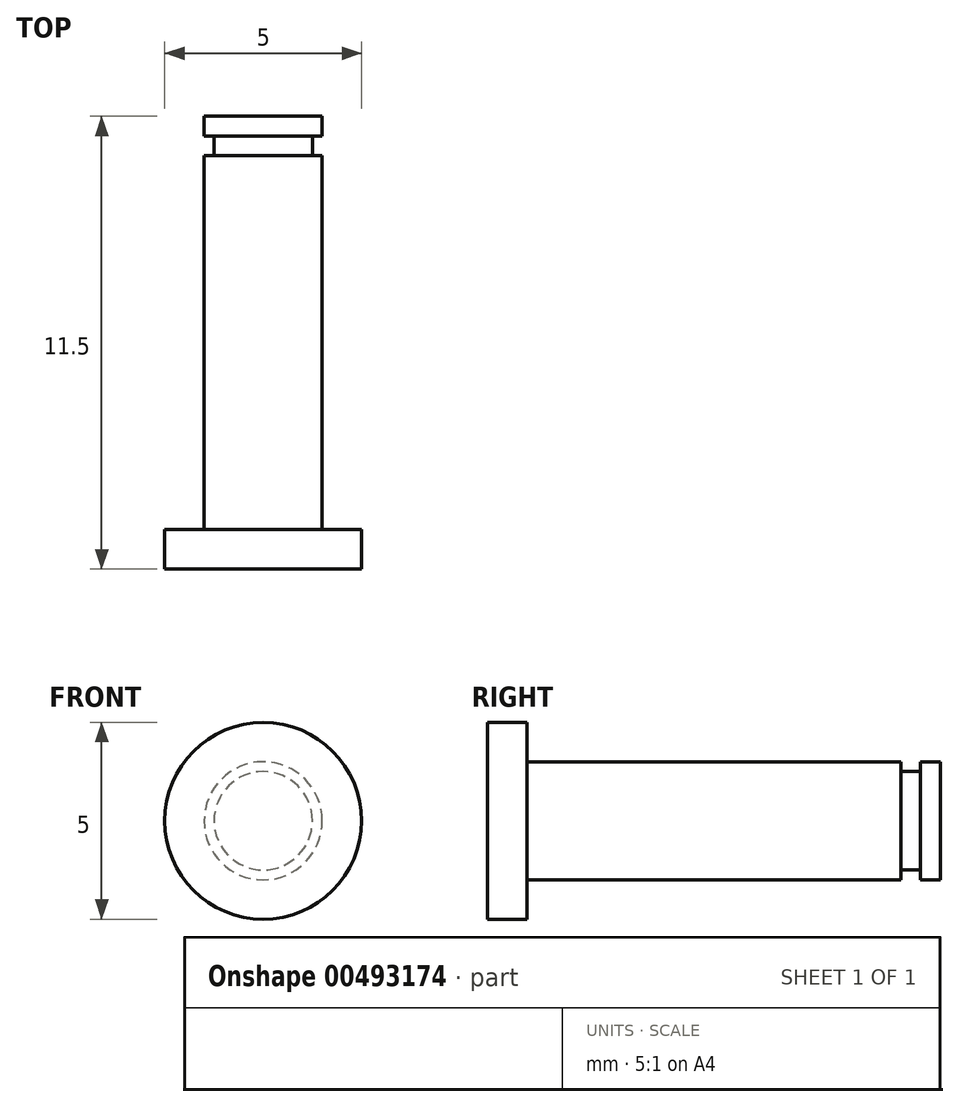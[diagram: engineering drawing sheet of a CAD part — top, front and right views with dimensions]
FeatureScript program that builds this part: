
annotation { "Feature Type Name" : "Feature", "Feature Type Description" : "" }
export const myFeature = defineFeature(function(context is Context, id is Id, definition is map)
    precondition{}
    {
        {
            var Q0;
            Q0=qCreatedBy(makeId("Front.planeOp"),FACE);
            var sketch = newSketch(context, id + "F0", { "sketchPlane" : qUnion([Q0])});
            skCircle(sketch, "E0", {"center": v(0, 0) * mm, "radius": 1.5 * mm});
            skSolve(sketch);
        }
        {
            var Q0;
            Q0=qSketchRegion(id+"F0",true);
            extrude(context, id + "F1", {"entities" : qUnion([Q0]), "depth" : 9.5 * mm});
        }
        {
            var Q0;
            Q0=makeQuery(id+"F1.opExtrude","CAP_FACE",FACE,{"disambiguationData":[OSD([sQuery(id+"F0.wireOp",EDGE,"E0")])],"isStart":false});
            var sketch = newSketch(context, id + "F2", { "sketchPlane" : qUnion([Q0])});
            skCircle(sketch, "E1", {"center": v(0, 0) * mm, "radius": 2.5 * mm});
            skSolve(sketch);
        }
        {
            var Q0;
            Q0=qSketchRegion(id+"F2",true);
            extrude(context, id + "F3", {"entities" : qUnion([Q0]), "operationType" : NewBodyOperationType.ADD, "depth" : 1 * mm});
        }
        {
            var Q0;
            Q0=makeQuery(id+"F1.opExtrude","CAP_FACE",FACE,{"disambiguationData":[OSD([sQuery(id+"F0.wireOp",EDGE,"E0")])],"isStart":true});
            var sketch = newSketch(context, id + "F4", { "sketchPlane" : qUnion([Q0])});
            skCircle(sketch, "E2", {"center": v(0, 0) * mm, "radius": 1.25 * mm});
            skSolve(sketch);
        }
        {
            var Q0;
            Q0=qSketchRegion(id+"F4",true);
            extrude(context, id + "F5", {"entities" : qUnion([Q0]), "operationType" : NewBodyOperationType.ADD, "depth" : .5 * mm});
        }
        {
            var Q0;
            Q0=makeQuery(id+"F5.opExtrude","CAP_FACE",FACE,{"disambiguationData":[OSD([sQuery(id+"F4.wireOp",EDGE,"E2")])],"isStart":false});
            var sketch = newSketch(context, id + "F6", { "sketchPlane" : qUnion([Q0])});
            skCircle(sketch, "E3", {"center": v(0, 0) * mm, "radius": 1.5 * mm});
            skSolve(sketch);
        }
        {
            var Q0;
            Q0=qSketchRegion(id+"F6",true);
            extrude(context, id + "F7", {"entities" : qUnion([Q0]), "operationType" : NewBodyOperationType.ADD, "depth" : .5 * mm});
        }
    });
